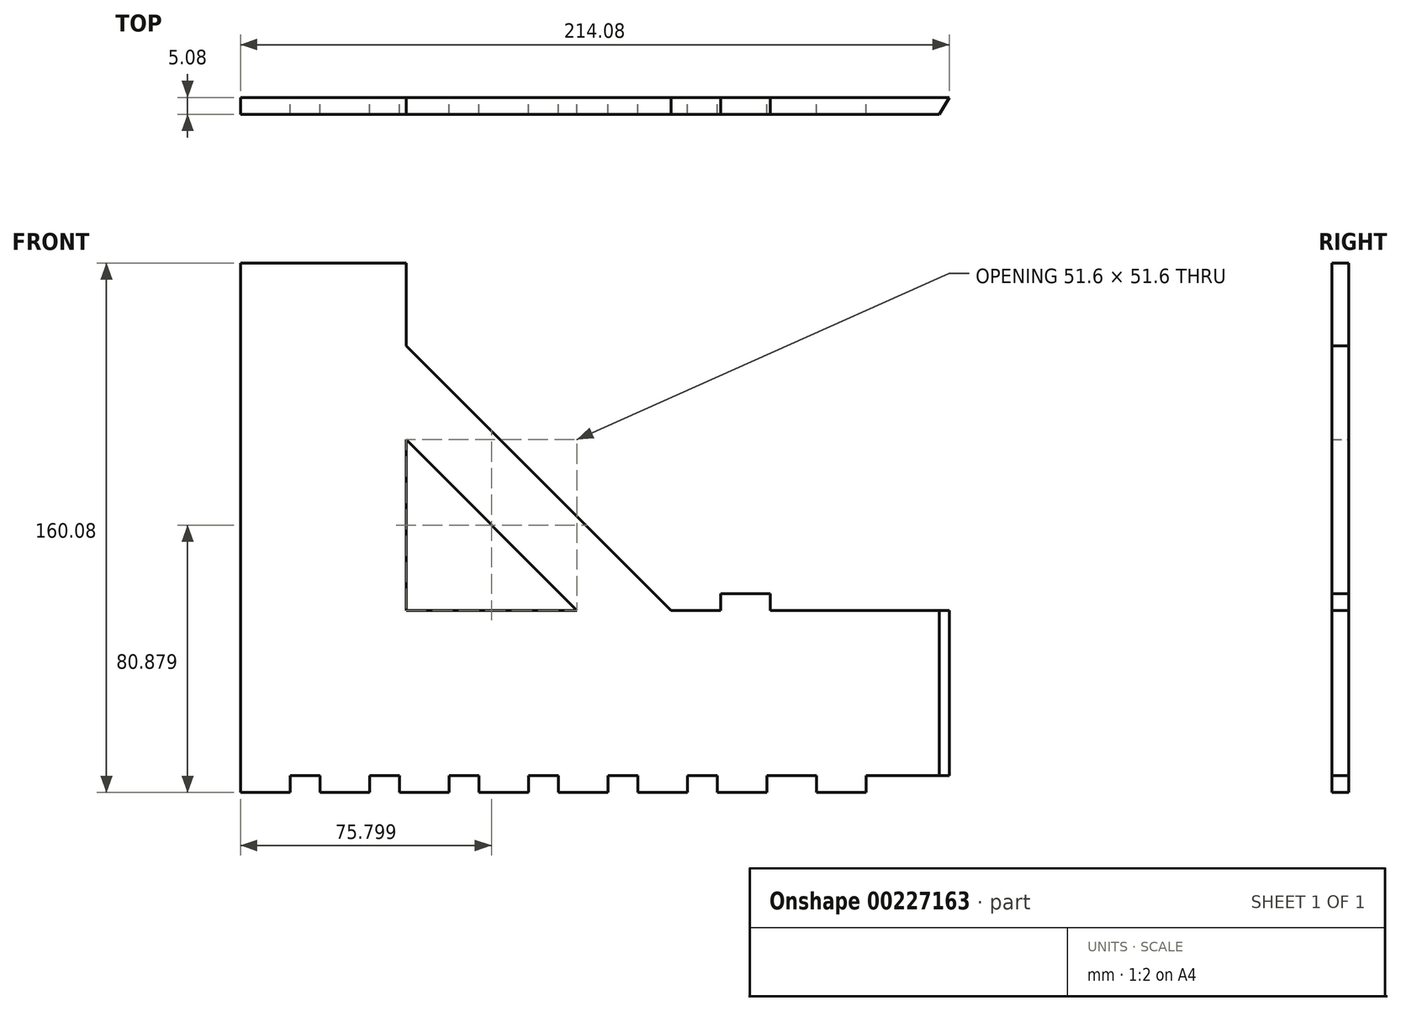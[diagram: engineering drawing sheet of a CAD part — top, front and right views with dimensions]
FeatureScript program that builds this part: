
annotation { "Feature Type Name" : "Feature", "Feature Type Description" : "" }
export const myFeature = defineFeature(function(context is Context, id is Id, definition is map)
    precondition{}
    {
        {
            var Q0;
            Q0=qCreatedBy(makeId("Front.planeOp"),FACE);
            var sketch = newSketch(context, id + "F0", { "sketchPlane" : qUnion([Q0])});
            skLineSegment(sketch, "E0", {"start": v(-32.42, 0) * mm, "end": v(-246.5, 0) * mm});
            skLineSegment(sketch, "E1", {"start": v(-246.5, 0) * mm, "end": v(-246.5, 130) * mm});
            skLineSegment(sketch, "E2", {"start": v(-246.5, 130) * mm, "end": v(-196.5, 130) * mm});
            skLineSegment(sketch, "E3", {"start": v(-196.5, 130) * mm, "end": v(-196.5, 50) * mm});
            skLineSegment(sketch, "E4", {"start": v(-196.5, 50) * mm, "end": v(-32.42, 50) * mm});
            skLineSegment(sketch, "E5", {"start": v(-196.5, 130) * mm, "end": v(-116.5, 50) * mm});
            skLineSegment(sketch, "E6", {"start": v(-196.5, 101.6) * mm, "end": v(-144.9, 50) * mm});
            skLineSegment(sketch, "E7", {"start": v(-246.5, 0) * mm, "end": v(-246.5, -5.08) * mm});
            skLineSegment(sketch, "E8", {"start": v(-246.5, -5.08) * mm, "end": v(-231.5, -5.08) * mm});
            skLineSegment(sketch, "E9", {"start": v(-231.5, -5.08) * mm, "end": v(-231.5, 0) * mm});
            skLineSegment(sketch, "E10.1.0.0", {"start": v(-207.5, -5.08) * mm, "end": v(-207.5, 0) * mm});
            skLineSegment(sketch, "E10.1.0.1", {"start": v(-222.5, -5.08) * mm, "end": v(-207.5, -5.08) * mm});
            skLineSegment(sketch, "E10.1.0.2", {"start": v(-222.5, 0) * mm, "end": v(-222.5, -5.08) * mm});
            skLineSegment(sketch, "E10.2.0.0", {"start": v(-183.5, -5.08) * mm, "end": v(-183.5, 0) * mm});
            skLineSegment(sketch, "E10.2.0.1", {"start": v(-198.5, -5.08) * mm, "end": v(-183.5, -5.08) * mm});
            skLineSegment(sketch, "E10.2.0.2", {"start": v(-198.5, 0) * mm, "end": v(-198.5, -5.08) * mm});
            skLineSegment(sketch, "E10.3.0.0", {"start": v(-159.5, -5.08) * mm, "end": v(-159.5, 0) * mm});
            skLineSegment(sketch, "E10.3.0.1", {"start": v(-174.5, -5.08) * mm, "end": v(-159.5, -5.08) * mm});
            skLineSegment(sketch, "E10.3.0.2", {"start": v(-174.5, 0) * mm, "end": v(-174.5, -5.08) * mm});
            skLineSegment(sketch, "E10.4.0.0", {"start": v(-135.5, -5.08) * mm, "end": v(-135.5, 0) * mm});
            skLineSegment(sketch, "E10.4.0.1", {"start": v(-150.5, -5.08) * mm, "end": v(-135.5, -5.08) * mm});
            skLineSegment(sketch, "E10.4.0.2", {"start": v(-150.5, 0) * mm, "end": v(-150.5, -5.08) * mm});
            skLineSegment(sketch, "E10.5.0.0", {"start": v(-111.5, -5.08) * mm, "end": v(-111.5, 0) * mm});
            skLineSegment(sketch, "E10.5.0.1", {"start": v(-126.5, -5.08) * mm, "end": v(-111.5, -5.08) * mm});
            skLineSegment(sketch, "E10.5.0.2", {"start": v(-126.5, 0) * mm, "end": v(-126.5, -5.08) * mm});
            skLineSegment(sketch, "E10.6.0.0", {"start": v(-87.5, -5.08) * mm, "end": v(-87.5, 0) * mm});
            skLineSegment(sketch, "E10.6.0.1", {"start": v(-102.5, -5.08) * mm, "end": v(-87.5, -5.08) * mm});
            skLineSegment(sketch, "E10.6.0.2", {"start": v(-102.5, 0) * mm, "end": v(-102.5, -5.08) * mm});
            skLineSegment(sketch, "E10.direction1", {"start": v(-246.5, -5.08) * mm, "end": v(-222.5, -5.08) * mm, "construction": true});
            skLineSegment(sketch, "E11", {"start": v(-32.42, 50) * mm, "end": v(-32.42, 0) * mm});
            skPoint(sketch, "E12.start.orphan", {"position": v(0, 50) * mm});
            skSolve(sketch);
        }
        {
            var Q0;
            Q0=qSketchRegion(id+"F0",true);
            extrude(context, id + "F1", {"entities" : qUnion([Q0]), "depth" : 5.08 * mm});
        }
        {
            var Q0;
            Q0=makeQuery(id+"F1.opExtrude","SWEPT_FACE",FACE,{"disambiguationData":[OSD([sQuery(id+"F0.wireOp",EDGE,"E2")])]});
            var Q1;
            Q1=makeQuery(id+"F1.opExtrude","SWEPT_FACE",FACE,{"disambiguationData":[OSD([sQuery(id+"F0.wireOp",EDGE,"0f3f7d79-0024-4810-854d-b7a6c9fa19c64.MirrorCS")])]});
            extrude(context, id + "F2", {"entities" : qUnion([Q0, Q1]), "operationType" : NewBodyOperationType.ADD, "depth" : 25 * mm});
        }
        {
            var Q0;
            {var subQ0=sQuery(id+"F0.wireOp",EDGE,"E0");Q0=makeQuery(id+"F1.opExtrude","SWEPT_FACE",FACE,{"disambiguationData":[OSD([subQ0]),TDD([makeQuery(id+"F0.imprint","IMPRINT",EDGE,{"disambiguationData":[TD([[makeQuery(id+"F0.imprint","INTERSECT",VERTEX,{"derivedFrom":[subQ0,sQuery(id+"F0.wireOp",EDGE,"E11")]}),-1.0]])],"derivedFrom":subQ0})])]});}
            var sketch = newSketch(context, id + "F3", { "sketchPlane" : qUnion([Q0])});
            skLineSegment(sketch, "E13", {"start": v(-35.35, 0) * mm, "end": v(-35.35, 5.08) * mm});
            skLineSegment(sketch, "E14", {"start": v(-35.35, 5.08) * mm, "end": v(-32.42, 0) * mm});
            skSolve(sketch);
        }
        {
            var Q0;
            {var subQ0=sQuery(id+"F3.wireOp",EDGE,"E14");Q0=makeQuery(id+"F3.imprint","IMPRINT",FACE,{"disambiguationData":[TD([[makeQuery(id+"F3.imprint","IMPRINT",EDGE,{"derivedFrom":subQ0}),1.0]])]});}
            extrude(context, id + "F4", {"entities" : qUnion([Q0]), "operationType" : NewBodyOperationType.REMOVE, "oppositeDirection" : true, "depth" : 55.7 * mm});
        }
        {
            var Q0;
            {var subQ0=sQuery(id+"F0.wireOp",EDGE,"E0");Q0=makeQuery(id+"F1.opExtrude","SWEPT_FACE",FACE,{"disambiguationData":[OSD([subQ0]),TDD([makeQuery(id+"F0.imprint","IMPRINT",EDGE,{"disambiguationData":[TD([[makeQuery(id+"F0.imprint","INTERSECT",VERTEX,{"derivedFrom":[subQ0,sQuery(id+"F0.wireOp",EDGE,"E11")]}),-1.0]])],"derivedFrom":subQ0})])]});}
            var sketch = newSketch(context, id + "F5", { "sketchPlane" : qUnion([Q0])});
            skLineSegment(sketch, "E15.bottom", {"start": v(-72.5, 5.08) * mm, "end": v(-57.5, 5.08) * mm});
            skLineSegment(sketch, "E15.top", {"start": v(-72.5, 0) * mm, "end": v(-57.5, 0) * mm});
            skLineSegment(sketch, "E15.right", {"start": v(-57.5, 5.08) * mm, "end": v(-57.5, 0) * mm});
            skLineSegment(sketch, "E16", {"start": v(-72.5, 5.08) * mm, "end": v(-72.5, 0) * mm});
            skPoint(sketch, "E15.left.start.orphan", {"position": v(-87.5, 5.08) * mm});
            skPoint(sketch, "E17.orphan", {"position": v(-87.5, 0) * mm});
            skSolve(sketch);
        }
        {
            var Q0;
            Q0 = qSketchRegion(id + "F5", true);
            extrude(context, id + "F6", {"entities" : qUnion([Q0]), "operationType" : NewBodyOperationType.ADD, "depth" : 5.08 * mm});
        }
        {
            var Q0;
            {var subQ0=sQuery(id+"F0.wireOp",EDGE,"E4");Q0=makeQuery(id+"F1.opExtrude","SWEPT_FACE",FACE,{"disambiguationData":[OSD([subQ0]),TDD([makeQuery(id+"F0.imprint","IMPRINT",EDGE,{"disambiguationData":[TD([[makeQuery(id+"F0.imprint","INTERSECT",VERTEX,{"derivedFrom":[subQ0,sQuery(id+"F0.wireOp",EDGE,"E11")]}),1.0]])],"derivedFrom":subQ0})])]});}
            var sketch = newSketch(context, id + "F7", { "sketchPlane" : qUnion([Q0])});
            skLineSegment(sketch, "E18.bottom", {"start": v(-101.5, 0) * mm, "end": v(-86.5, 0) * mm});
            skLineSegment(sketch, "E18.top", {"start": v(-101.5, -5.08) * mm, "end": v(-86.5, -5.08) * mm});
            skLineSegment(sketch, "E18.right", {"start": v(-86.5, 0) * mm, "end": v(-86.5, -5.08) * mm});
            skLineSegment(sketch, "E19", {"start": v(-101.5, 0) * mm, "end": v(-101.5, -5.08) * mm});
            skPoint(sketch, "E18.left.end.orphan", {"position": v(-116.5, -5.08) * mm});
            skPoint(sketch, "E18.left.start.orphan", {"position": v(-116.5, 0) * mm});
            skSolve(sketch);
        }
        {
            var Q0;
            Q0 = qSketchRegion(id + "F7", true);
            extrude(context, id + "F8", {"entities" : qUnion([Q0]), "operationType" : NewBodyOperationType.ADD, "depth" : 5.08 * mm});
        }
    });
